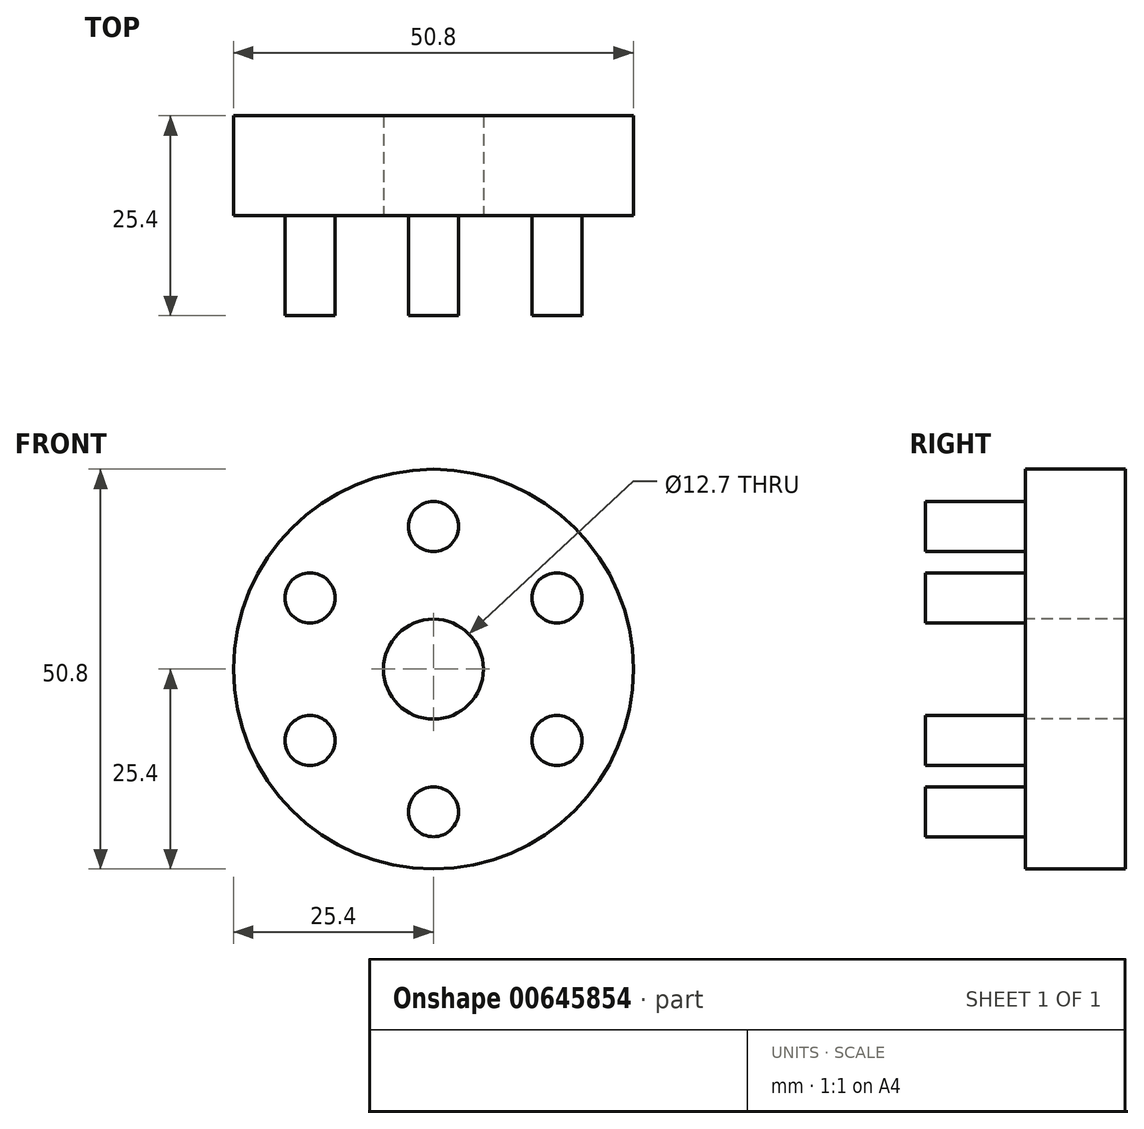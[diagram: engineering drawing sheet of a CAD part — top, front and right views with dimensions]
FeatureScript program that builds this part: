
annotation { "Feature Type Name" : "Feature", "Feature Type Description" : "" }
export const myFeature = defineFeature(function(context is Context, id is Id, definition is map)
    precondition{}
    {
        {
            var Q0;
            Q0=qCreatedBy(makeId("Front.planeOp"),FACE);
            var sketch = newSketch(context, id + "F0", { "sketchPlane" : qUnion([Q0])});
            skCircle(sketch, "E0", {"center": v(0, 0) * mm, "radius": 25.4 * mm});
            skSolve(sketch);
        }
        {
            var Q0;
            Q0 = qSketchRegion(id + "F0", true);
            extrude(context, id + "F1", {"entities" : qUnion([Q0]), "depth" : 12.7 * mm, "offsetDistance" : 25.4 * mm});
        }
        {
            var Q0;
            Q0=makeQuery(id+"F1.opExtrude","CAP_FACE",FACE,{"disambiguationData":[OSD([sQuery(id+"F0.wireOp",EDGE,"E0")])],"isStart":false});
            var sketch = newSketch(context, id + "F2", { "sketchPlane" : qUnion([Q0])});
            skCircle(sketch, "E1", {"center": v(0, 0) * mm, "radius": 6.35 * mm});
            skSolve(sketch);
        }
        {
            var Q0;
            Q0 = qSketchRegion(id + "F2", true);
            extrude(context, id + "F3", {"entities" : qUnion([Q0]), "operationType" : NewBodyOperationType.REMOVE, "oppositeDirection" : true, "depth" : 50.8 * mm, "offsetDistance" : 25.4 * mm});
        }
        {
            var Q0;
            Q0=makeQuery(id+"F1.opExtrude","CAP_FACE",FACE,{"disambiguationData":[OSD([sQuery(id+"F0.wireOp",EDGE,"E0")])],"isStart":false});
            var sketch = newSketch(context, id + "F4", { "sketchPlane" : qUnion([Q0])});
            skCircle(sketch, "E2", {"center": v(0, 18.11) * mm, "radius": 3.18 * mm});
            skCircle(sketch, "E3.1.0", {"center": v(-15.69, 9.06) * mm, "radius": 3.18 * mm});
            skCircle(sketch, "E3.2.0", {"center": v(-15.69, -9.06) * mm, "radius": 3.18 * mm});
            skCircle(sketch, "E3.3.0", {"center": v(0, -18.11) * mm, "radius": 3.18 * mm});
            skCircle(sketch, "E3.4.0", {"center": v(15.69, -9.06) * mm, "radius": 3.18 * mm});
            skCircle(sketch, "E3.5.0", {"center": v(15.69, 9.06) * mm, "radius": 3.18 * mm});
            skPoint(sketch, "E3.center", {"position": v(0, 0) * mm});
            skSolve(sketch);
        }
        {
            var Q0;
            Q0 = qSketchRegion(id + "F4", true);
            extrude(context, id + "F5", {"entities" : qUnion([Q0]), "operationType" : NewBodyOperationType.ADD, "depth" : 12.7 * mm, "offsetDistance" : 25.4 * mm});
        }
    });
